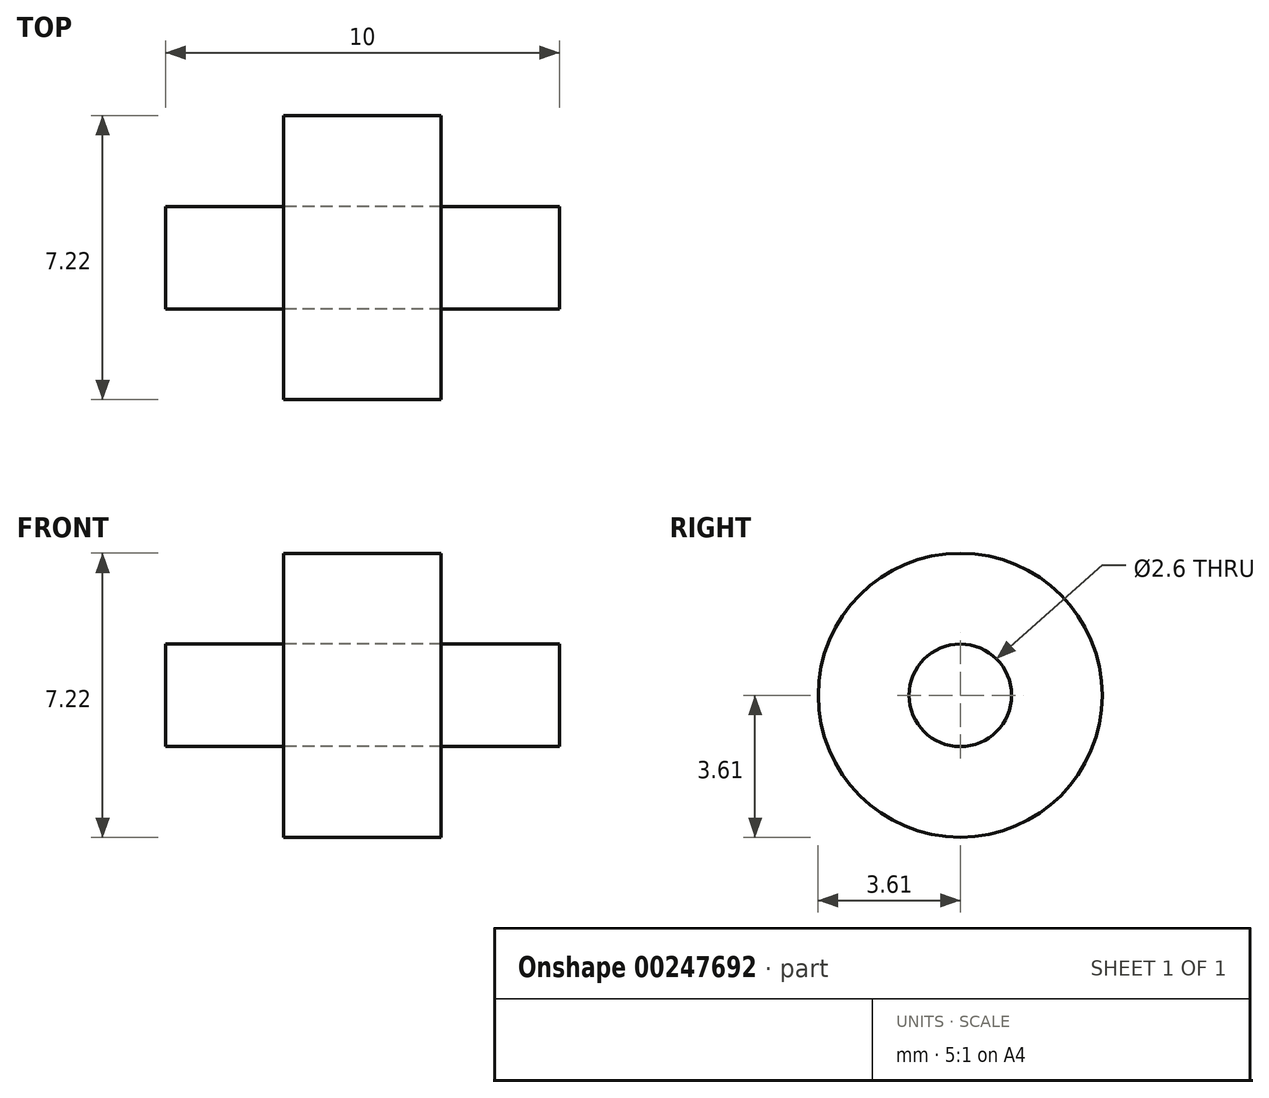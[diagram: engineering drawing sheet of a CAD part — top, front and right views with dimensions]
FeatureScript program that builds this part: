
annotation { "Feature Type Name" : "Feature", "Feature Type Description" : "" }
export const myFeature = defineFeature(function(context is Context, id is Id, definition is map)
    precondition{}
    {
        {
            var Q0;
            Q0=qCreatedBy(makeId("Right.planeOp"),FACE);
            var sketch = newSketch(context, id + "F0", { "sketchPlane" : qUnion([Q0])});
            skCircle(sketch, "E0", {"center": v(0, 0) * mm, "radius": 3.6 * mm});
            skCircle(sketch, "E1", {"center": v(0, 0) * mm, "radius": 1.3 * mm});
            skSolve(sketch);
        }
        {
            var Q0;
            Q0 = qSketchRegion(id + "F0", true);
            extrude(context, id + "F1", {"entities" : qUnion([Q0]), "depth" : 4 * mm});
        }
        {
            var Q0;
            Q0=makeQuery(id+"F0.imprint","IMPRINT",FACE,{"disambiguationData":[TD([[makeQuery(id+"F0.imprint","IMPRINT",EDGE,{"derivedFrom":sQuery(id+"F0.wireOp",EDGE,"E1")}),1.0]])]});
            extrude(context, id + "F2", {"entities" : qUnion([Q0]), "depth" : 7 * mm, "hasSecondDirection" : true, "secondDirectionOppositeDirection" : true, "secondDirectionDepth" : 3 * mm});
        }
    });
